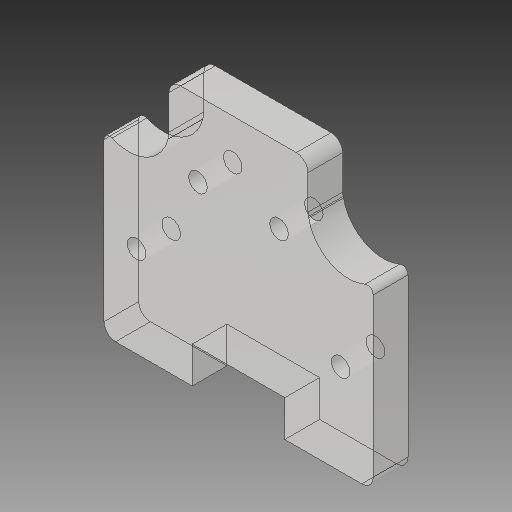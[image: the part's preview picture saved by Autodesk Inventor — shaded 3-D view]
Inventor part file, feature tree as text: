
AUTODESK INVENTOR PART (.ipt)
format: ipt  version: 2018 (Build 220112000, 112)  size: 163,840 bytes
history: native  units: mm
features: sketch x4, other x3, plane x1
ambient origin geometry x8: Origin, YZ Plane, XZ Plane, XY Plane, X Axis, Y Axis, Z Axis, Center Point
bodies: Solid1 (feature_tree)
feature tree (8):
  other  "Hotend Slide Part3_MIR.ipt"
  other  "Solid1::Hotend Slide Part3_MIR.ipt"
  other  "TaggingFeature1"
  sketch  "Sketch1"  dims[d0=10.0mm]
  sketch  "Sketch2"
  sketch  "Sketch3"
  sketch  "Sketch4"
  plane  "Work Plane1"
